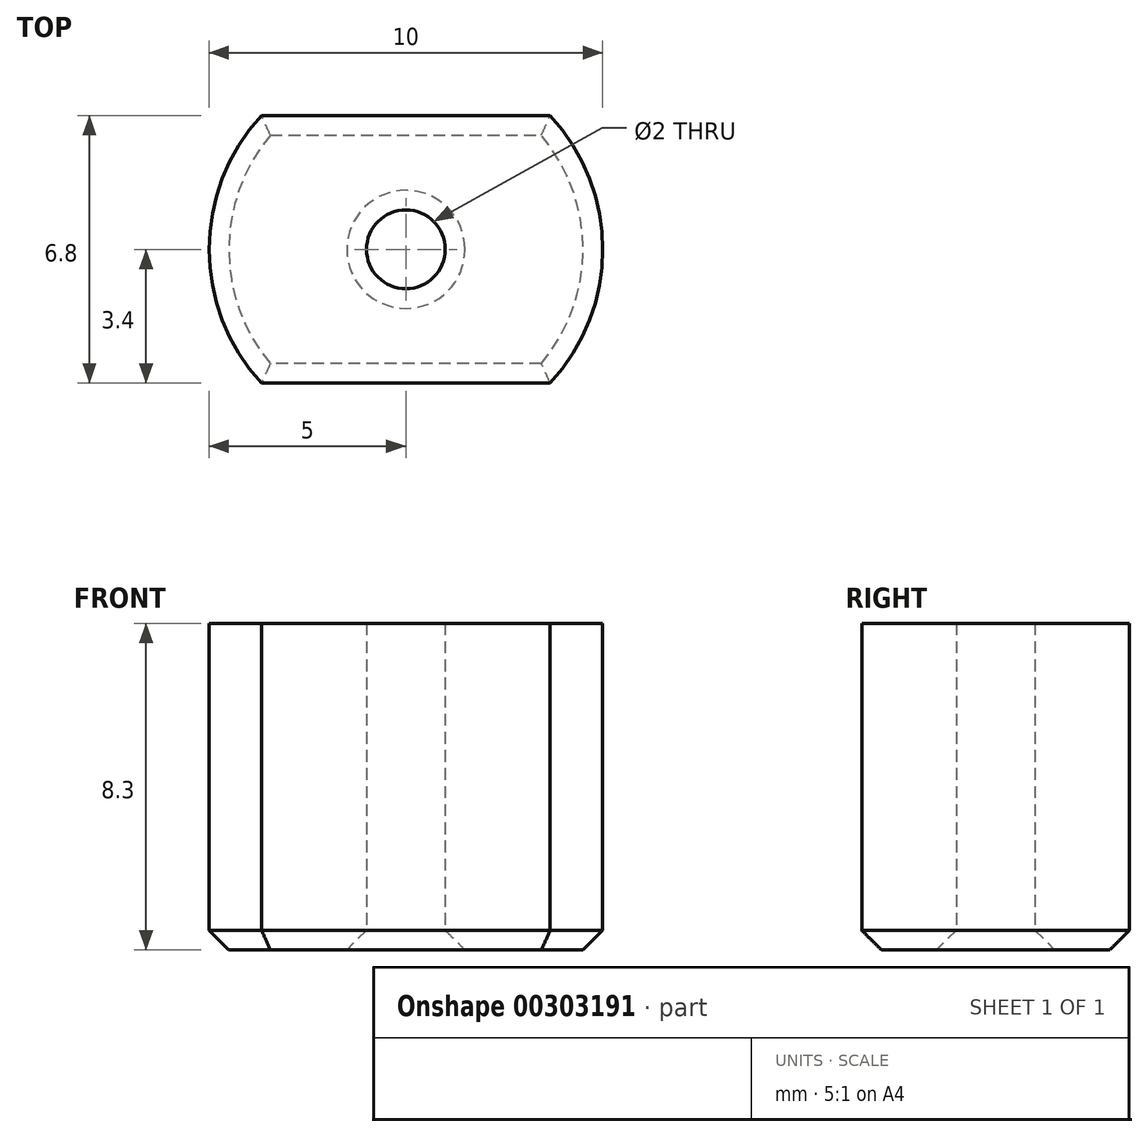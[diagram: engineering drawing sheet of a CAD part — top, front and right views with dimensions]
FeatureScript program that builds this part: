
annotation { "Feature Type Name" : "Feature", "Feature Type Description" : "" }
export const myFeature = defineFeature(function(context is Context, id is Id, definition is map)
    precondition{}
    {
        {
            var Q0;
            Q0=qCreatedBy(makeId("Top.planeOp"),FACE);
            var sketch = newSketch(context, id + "F0", { "sketchPlane" : qUnion([Q0])});
            skCircle(sketch, "E0", {"center": v(0, 0) * mm, "radius": 1 * mm});
            skArc(sketch, "E1", {"start": v(-3.67, 3.4) * mm, "mid": v(-5, 0) * mm, "end": v(-3.67, -3.4) * mm});
            skLineSegment(sketch, "E2", {"start": v(-3.67, 3.4) * mm, "end": v(3.67, 3.4) * mm});
            skLineSegment(sketch, "E3", {"start": v(-3.67, -3.4) * mm, "end": v(3.67, -3.4) * mm});
            skArc(sketch, "E4.trimOffspring", {"start": v(3.67, -3.4) * mm, "mid": v(5, 0) * mm, "end": v(3.67, 3.4) * mm});
            skSolve(sketch);
        }
        {
            var Q0;
            Q0 = qSketchRegion(id + "F0", true);
            extrude(context, id + "F1", {"entities" : qUnion([Q0]), "depth" : 8.3 * mm});
        }
        {
            var Q0;
            Q0=makeQuery(id+"F1.opExtrude","CAP_FACE",FACE,{"disambiguationData":[OSD([sQuery(id+"F0.wireOp",EDGE,"E0"),sQuery(id+"F0.wireOp",EDGE,"E1"),sQuery(id+"F0.wireOp",EDGE,"E2"),sQuery(id+"F0.wireOp",EDGE,"E3"),sQuery(id+"F0.wireOp",EDGE,"E4.trimOffspring")])],"isStart":true});
            chamfer(context, id + "F2", {"entities" : qUnion([Q0]), "width" : 0.5 * mm, "tangentPropagation" : true});
        }
    });
